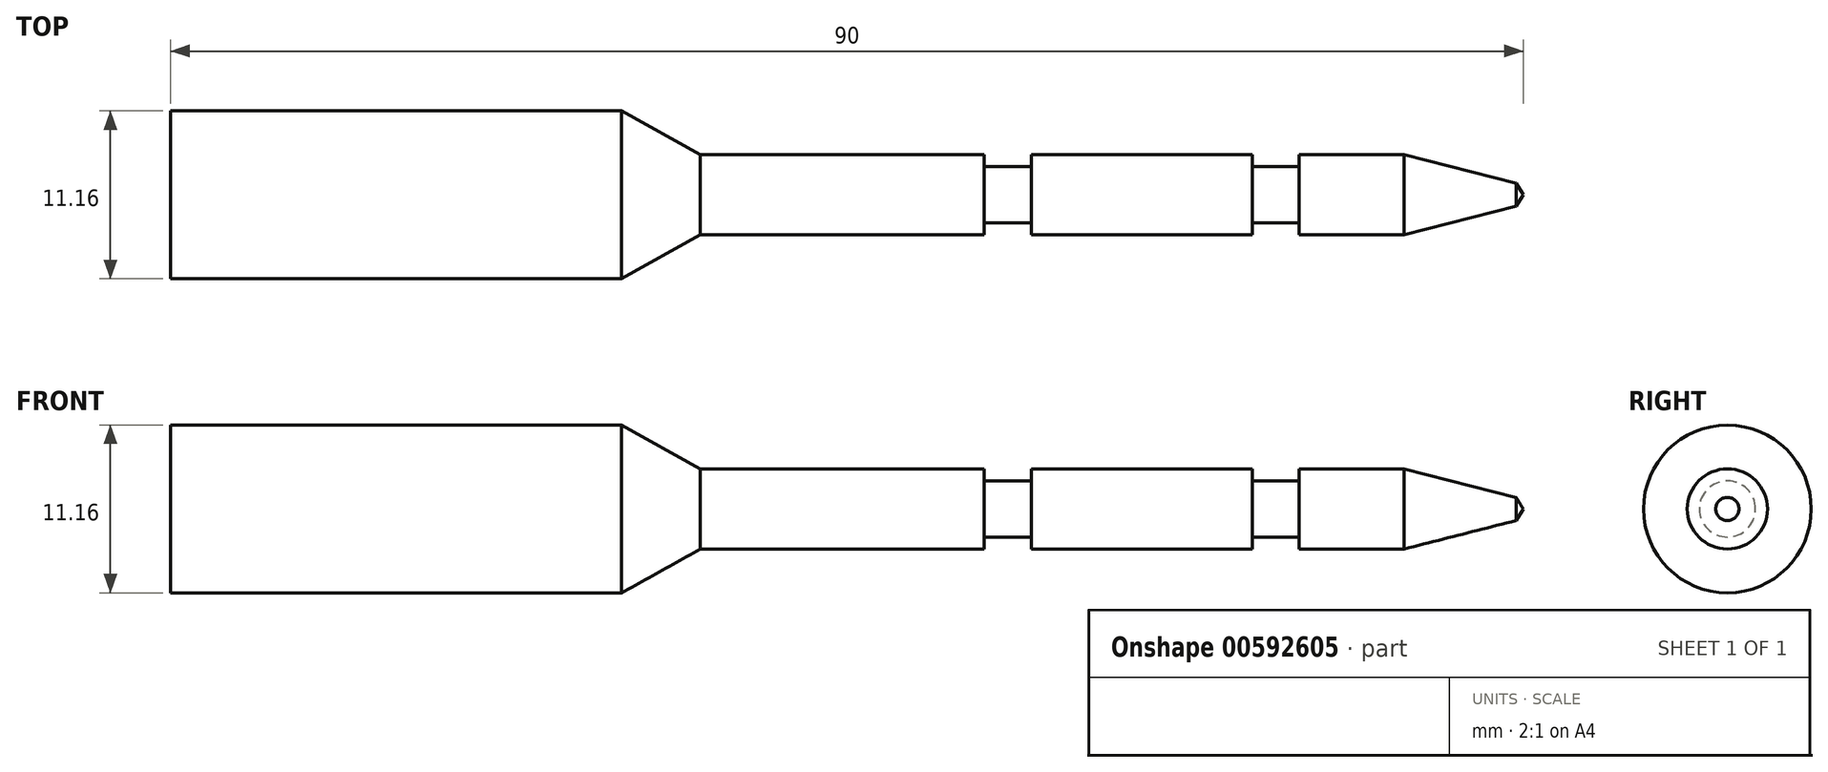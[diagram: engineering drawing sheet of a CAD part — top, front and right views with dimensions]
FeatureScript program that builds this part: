
annotation { "Feature Type Name" : "Feature", "Feature Type Description" : "" }
export const myFeature = defineFeature(function(context is Context, id is Id, definition is map)
    precondition{}
    {
        {
            var Q0;
            Q0=qCreatedBy(makeId("Front.planeOp"),FACE);
            var sketch = newSketch(context, id + "F0", { "sketchPlane" : qUnion([Q0])});
            skLineSegment(sketch, "E0", {"start": v(0, 5.58) * mm, "end": v(30, 5.58) * mm});
            skLineSegment(sketch, "E1", {"start": v(30, 5.58) * mm, "end": v(35.24, 2.67) * mm});
            skLineSegment(sketch, "E2", {"start": v(35.24, 2.67) * mm, "end": v(54.14, 2.67) * mm});
            skLineSegment(sketch, "E3", {"start": v(54.14, 2.67) * mm, "end": v(54.14, 1.87) * mm});
            skLineSegment(sketch, "E4", {"start": v(54.14, 1.87) * mm, "end": v(57.27, 1.87) * mm});
            skLineSegment(sketch, "E5", {"start": v(57.27, 1.87) * mm, "end": v(57.27, 2.67) * mm});
            skLineSegment(sketch, "E6", {"start": v(57.27, 2.67) * mm, "end": v(71.97, 2.67) * mm});
            skLineSegment(sketch, "E7", {"start": v(71.97, 1.87) * mm, "end": v(71.97, 2.67) * mm});
            skLineSegment(sketch, "E8", {"start": v(75.07, 1.87) * mm, "end": v(71.97, 1.87) * mm});
            skLineSegment(sketch, "E9", {"start": v(75.07, 2.67) * mm, "end": v(75.07, 1.87) * mm});
            skLineSegment(sketch, "E10", {"start": v(75.07, 2.67) * mm, "end": v(82.07, 2.67) * mm});
            skLineSegment(sketch, "E11", {"start": v(82.07, 2.67) * mm, "end": v(89.53, 0.77) * mm});
            skLineSegment(sketch, "E12", {"start": v(89.53, 0.77) * mm, "end": v(90, 0) * mm});
            skLineSegment(sketch, "E13", {"start": v(90, 0) * mm, "end": v(0, 0) * mm});
            skLineSegment(sketch, "E14", {"start": v(0, 0) * mm, "end": v(0, 5.58) * mm});
            skSolve(sketch);
        }
        {
            var Q0;
            Q0=makeQuery(id+"F0.imprint","IMPRINT",FACE,{"disambiguationData":[TD([[makeQuery(id+"F0.imprint","IMPRINT",EDGE,{"derivedFrom":sQuery(id+"F0.wireOp",EDGE,"E0")}),-1.0]])]});
            var Q1;
            Q1=sQuery(id+"F0.wireOp",EDGE,"E13");
            revolve(context, id + "F1", {"entities" : qUnion([Q0]), "axis" : qUnion([Q1]), "revolveType" : RevolveType.FULL});
        }
    });
